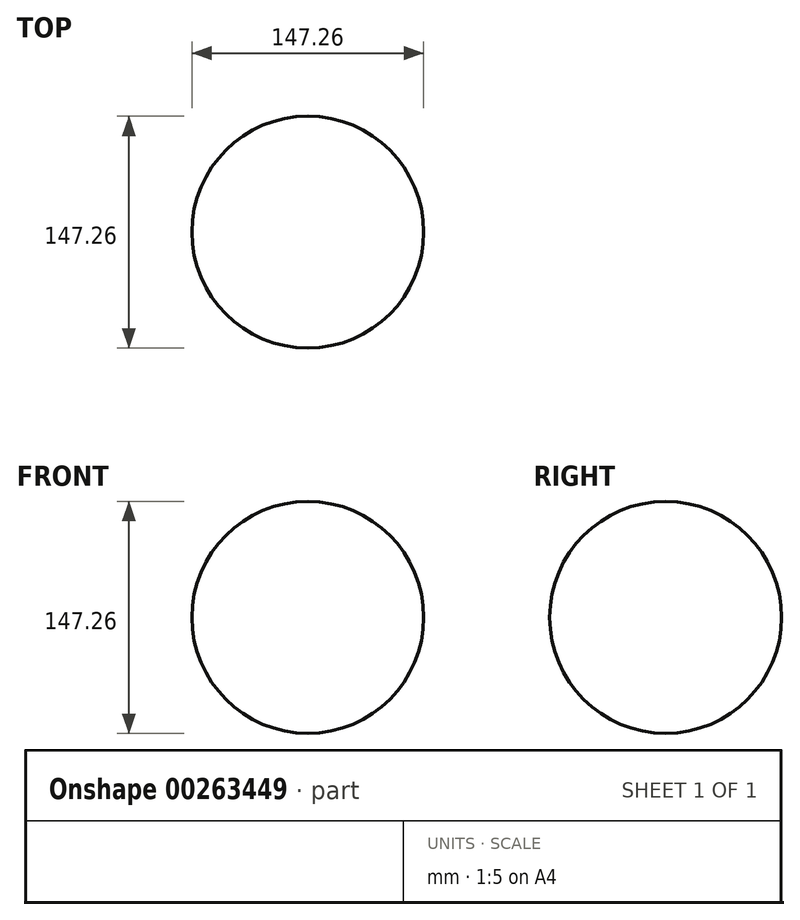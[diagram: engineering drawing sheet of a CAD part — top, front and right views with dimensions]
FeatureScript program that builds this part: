
annotation { "Feature Type Name" : "Feature", "Feature Type Description" : "" }
export const myFeature = defineFeature(function(context is Context, id is Id, definition is map)
    precondition{}
    {
        {
            var Q0;
            Q0=qCreatedBy(makeId("Front.planeOp"),FACE);
            var sketch = newSketch(context, id + "F0", { "sketchPlane" : qUnion([Q0])});
            skLineSegment(sketch, "E0", {"start": v(0, 76.45) * mm, "end": v(0, -76) * mm, "construction": true});
            skArc(sketch, "E1", {"start": v(0, 73.63) * mm, "mid": v(-73.63, 0) * mm, "end": v(0, -73.63) * mm});
            skSolve(sketch);
        }
        {
            var Q0;
            Q0=sQuery(id+"F0.wireOp",EDGE,"E1");
            var Q1;
            Q1=sQuery(id+"F0.wireOp",EDGE,"E0");
            revolve(context, id + "F1", {"bodyType" : ToolBodyType.SURFACE, "surfaceEntities" : qUnion([Q0]), "axis" : qUnion([Q1]), "revolveType" : RevolveType.FULL});
        }
    });
